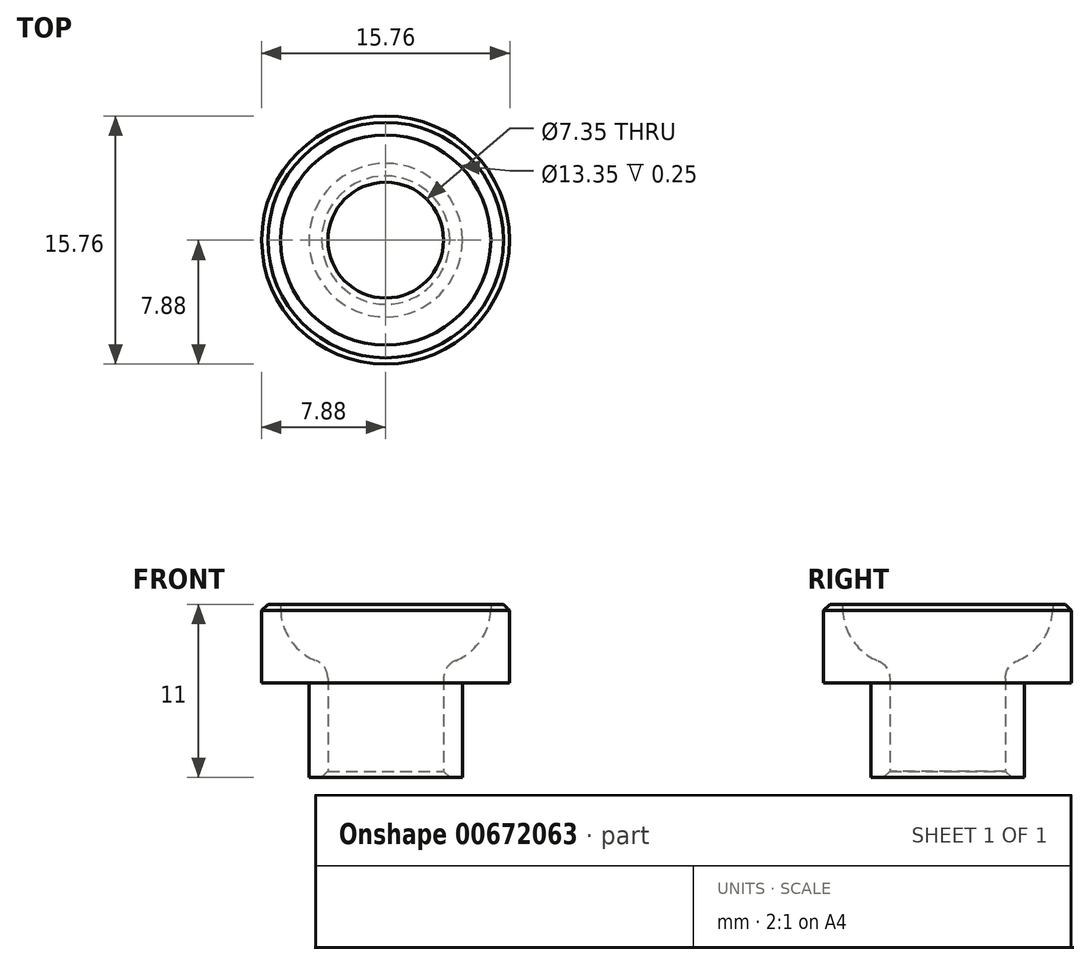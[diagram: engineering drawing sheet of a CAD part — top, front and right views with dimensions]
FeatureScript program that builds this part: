
annotation { "Feature Type Name" : "Feature", "Feature Type Description" : "" }
export const myFeature = defineFeature(function(context is Context, id is Id, definition is map)
    precondition{}
    {
        {
            var Q0;
            Q0=qCreatedBy(makeId("Front.planeOp"),FACE);
            var sketch = newSketch(context, id + "F0", { "sketchPlane" : qUnion([Q0])});
            skLineSegment(sketch, "E0", {"start": v(-4.88, 0) * mm, "end": v(-4.88, 6) * mm});
            skLineSegment(sketch, "E1", {"start": v(-4.88, 6) * mm, "end": v(-7.88, 6) * mm});
            skLineSegment(sketch, "E2", {"start": v(-7.88, 6) * mm, "end": v(-7.88, 11) * mm});
            skLineSegment(sketch, "E3", {"start": v(-7.88, 11) * mm, "end": v(-6.68, 11) * mm});
            skLineSegment(sketch, "E4", {"start": v(-6.68, 11) * mm, "end": v(-6.68, 7.2) * mm});
            skLineSegment(sketch, "E5", {"start": v(-6.68, 7.2) * mm, "end": v(-3.68, 7.2) * mm});
            skLineSegment(sketch, "E6", {"start": v(-3.68, 7.2) * mm, "end": v(-3.67, 0) * mm});
            skLineSegment(sketch, "E7", {"start": v(-3.67, 0) * mm, "end": v(-4.88, 0) * mm});
            skLineSegment(sketch, "E8", {"start": v(0, 0) * mm, "end": v(0, 11) * mm});
            skSolve(sketch);
        }
        {
            var Q0;
            Q0=makeQuery(id+"F0.imprint","IMPRINT",FACE,{"disambiguationData":[TD([[makeQuery(id+"F0.imprint","IMPRINT",EDGE,{"derivedFrom":sQuery(id+"F0.wireOp",EDGE,"E0")}),-1.0]])]});
            var Q1;
            Q1=sQuery(id+"F0.wireOp",EDGE,"E8");
            revolve(context, id + "F1", {"entities" : qUnion([Q0]), "axis" : qUnion([Q1]), "revolveType" : RevolveType.FULL});
        }
        {
            var Q0;
            Q0=makeQuery(id+"F1.opRevolve","SWEPT_EDGE",EDGE,{"disambiguationData":[OSD([sQuery(id+"F0.wireOp",EDGE,"E4"),sQuery(id+"F0.wireOp",EDGE,"E5")])]});
            fillet(context, id + "F2", {"entities" : qUnion([Q0]), "radius" : 3.6 * mm, "tangentPropagation" : true, "allowEdgeOverflow" : false});
        }
        {
            var Q0;
            Q0=makeQuery(id+"F2.opFillet","BLEND_EDGE",EDGE,{"blendedFrom":[makeQuery(id+"F1.opRevolve","SWEPT_EDGE",EDGE,{"disambiguationData":[OSD([sQuery(id+"F0.wireOp",EDGE,"E4"),sQuery(id+"F0.wireOp",EDGE,"E5")])]}),makeQuery(id+"F1.opRevolve","SWEPT_FACE",FACE,{"disambiguationData":[OSD([sQuery(id+"F0.wireOp",EDGE,"E6")])]})],"blendedInto":[makeQuery(id+"F1.opRevolve","SWEPT_FACE",FACE,{"disambiguationData":[OSD([sQuery(id+"F0.wireOp",EDGE,"E6")])]})]});
            fillet(context, id + "F3", {"entities" : qUnion([Q0]), "radius" : 1.2 * mm, "tangentPropagation" : true, "allowEdgeOverflow" : false});
        }
        {
            var Q0;
            Q0=makeQuery(id+"F1.opRevolve","SWEPT_EDGE",EDGE,{"disambiguationData":[OSD([sQuery(id+"F0.wireOp",EDGE,"E2"),sQuery(id+"F0.wireOp",EDGE,"E3")])]});
            var Q1;
            Q1=makeQuery(id+"F1.opRevolve","SWEPT_EDGE",EDGE,{"disambiguationData":[OSD([sQuery(id+"F0.wireOp",EDGE,"E6"),sQuery(id+"F0.wireOp",EDGE,"E7")])]});
            chamfer(context, id + "F4", {"entities" : qUnion([Q0, Q1]), "width" : .4 * mm, "tangentPropagation" : true});
        }
    });
